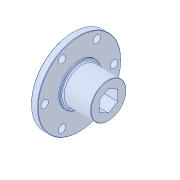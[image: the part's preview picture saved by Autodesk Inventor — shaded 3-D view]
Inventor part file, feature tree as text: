
AUTODESK INVENTOR PART (.ipt)
format: ipt  version: 2018 (Build 220112000, 112)  size: 142,336 bytes
history: native  units: in
note: dims shown in document units (in); Inventor stores cm internally (conversion verified against a paired STEP export)
features: chamfer x1
ambient origin geometry x8: Origin, YZ Plane, XZ Plane, XY Plane, X Axis, Y Axis, Z Axis, Center Point
bodies: Solid1 (feature_tree)
feature tree (1):
  chamfer  "Chamfer3"  [1 undecoded]
note: 1 required parameter value undecoded (feature->parameter linkage not recoverable at this tier; creation-order binding heuristic only, values carry confidence <= 0.55)
